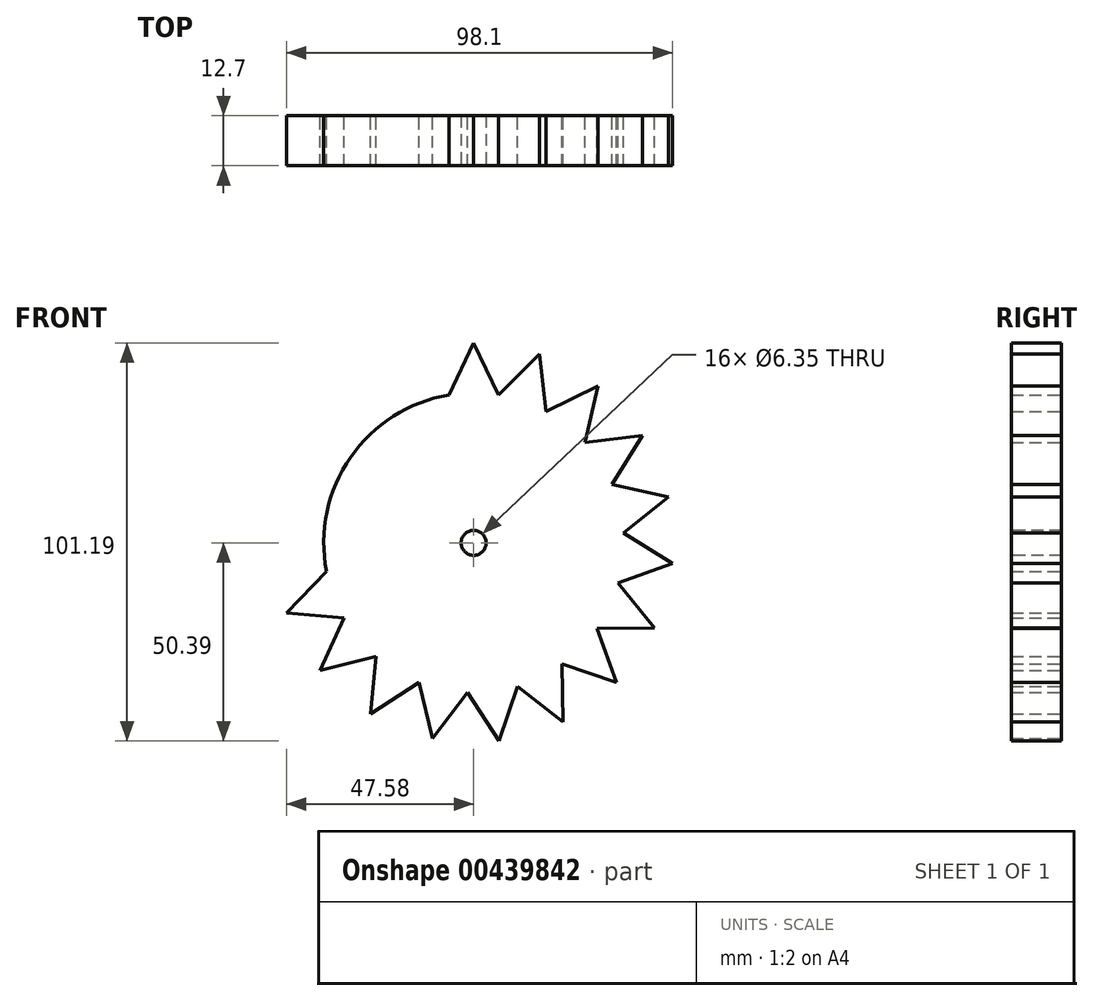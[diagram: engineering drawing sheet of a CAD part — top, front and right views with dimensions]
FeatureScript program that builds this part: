
annotation { "Feature Type Name" : "Feature", "Feature Type Description" : "" }
export const myFeature = defineFeature(function(context is Context, id is Id, definition is map)
    precondition{}
    {
        {
            var Q0;
            Q0=qCreatedBy(makeId("Front.planeOp"),FACE);
            var sketch = newSketch(context, id + "F0", { "sketchPlane" : qUnion([Q0])});
            skCircle(sketch, "E0", {"center": v(0, 0) * mm, "radius": 38.1 * mm});
            skPoint(sketch, "E1", {"position": v(0, 38.1) * mm});
            skPoint(sketch, "E2", {"position": v(12.52, 35.98) * mm});
            skPoint(sketch, "E3", {"position": v(23.65, 29.87) * mm});
            skPoint(sketch, "E4", {"position": v(32.16, 20.43) * mm});
            skPoint(sketch, "E5", {"position": v(37.09, 8.73) * mm});
            skPoint(sketch, "E6", {"position": v(37.9, -3.97) * mm});
            skPoint(sketch, "E7", {"position": v(34.48, -16.2) * mm});
            skPoint(sketch, "E8", {"position": v(27.24, -26.64) * mm});
            skPoint(sketch, "E9", {"position": v(16.97, -34.11) * mm});
            skPoint(sketch, "E10", {"position": v(4.82, -37.8) * mm});
            skPoint(sketch, "E11", {"position": v(-7.87, -37.28) * mm});
            skPoint(sketch, "E12", {"position": v(-19.68, -32.62) * mm});
            skPoint(sketch, "E13", {"position": v(-29.31, -24.34) * mm});
            skPoint(sketch, "E14", {"position": v(-35.68, -13.35) * mm});
            skLineSegment(sketch, "E15", {"start": v(0, 38.1) * mm, "end": v(0, 50.8) * mm});
            skLineSegment(sketch, "E16", {"start": v(0, 0) * mm, "end": v(12.52, 35.98) * mm});
            skLineSegment(sketch, "E17", {"start": v(0, 0) * mm, "end": v(23.65, 29.87) * mm});
            skLineSegment(sketch, "E18", {"start": v(0, 0) * mm, "end": v(32.16, 20.43) * mm});
            skLineSegment(sketch, "E19", {"start": v(0, 0) * mm, "end": v(37.09, 8.73) * mm});
            skLineSegment(sketch, "E20", {"start": v(0, 0) * mm, "end": v(37.9, -3.97) * mm});
            skLineSegment(sketch, "E21", {"start": v(0, 0) * mm, "end": v(34.48, -16.2) * mm});
            skLineSegment(sketch, "E22", {"start": v(0, 0) * mm, "end": v(27.24, -26.64) * mm});
            skLineSegment(sketch, "E23", {"start": v(0, 0) * mm, "end": v(16.97, -34.11) * mm});
            skLineSegment(sketch, "E24", {"start": v(0, 0) * mm, "end": v(4.82, -37.8) * mm});
            skLineSegment(sketch, "E25", {"start": v(0, 0) * mm, "end": v(-7.87, -37.28) * mm});
            skLineSegment(sketch, "E26", {"start": v(0, 0) * mm, "end": v(-19.68, -32.62) * mm});
            skLineSegment(sketch, "E27", {"start": v(0, 0) * mm, "end": v(-29.31, -24.34) * mm});
            skLineSegment(sketch, "E28", {"start": v(0, 0) * mm, "end": v(-35.68, -13.35) * mm});
            skLineSegment(sketch, "E29", {"start": v(12.52, 35.98) * mm, "end": v(16.7, 47.98) * mm});
            skLineSegment(sketch, "E30", {"start": v(23.65, 29.87) * mm, "end": v(31.54, 39.82) * mm});
            skLineSegment(sketch, "E31", {"start": v(32.16, 20.43) * mm, "end": v(42.87, 27.25) * mm});
            skLineSegment(sketch, "E32", {"start": v(37.09, 8.73) * mm, "end": v(49.45, 11.64) * mm});
            skLineSegment(sketch, "E33", {"start": v(34.48, -16.2) * mm, "end": v(45.98, -21.6) * mm});
            skLineSegment(sketch, "E34", {"start": v(27.24, -26.64) * mm, "end": v(36.32, -35.52) * mm});
            skLineSegment(sketch, "E35", {"start": v(16.97, -34.11) * mm, "end": v(22.63, -45.48) * mm});
            skLineSegment(sketch, "E36", {"start": v(4.82, -37.8) * mm, "end": v(6.43, -50.4) * mm});
            skLineSegment(sketch, "E37", {"start": v(-7.87, -37.28) * mm, "end": v(-10.5, -49.7) * mm});
            skLineSegment(sketch, "E38", {"start": v(-19.68, -32.62) * mm, "end": v(-26.25, -43.5) * mm});
            skLineSegment(sketch, "E39", {"start": v(-29.31, -24.34) * mm, "end": v(-39.08, -32.45) * mm});
            skLineSegment(sketch, "E40", {"start": v(-35.68, -13.35) * mm, "end": v(-47.58, -17.8) * mm});
            skLineSegment(sketch, "E41", {"start": v(37.9, -3.97) * mm, "end": v(50.52, -5.3) * mm});
            skPoint(sketch, "E42", {"position": v(-6.33, 37.57) * mm});
            skPoint(sketch, "E43", {"position": v(6.33, 37.57) * mm});
            skPoint(sketch, "E44", {"position": v(18.32, 33.4) * mm});
            skPoint(sketch, "E45", {"position": v(28.29, 25.53) * mm});
            skPoint(sketch, "E46", {"position": v(35.1, 14.81) * mm});
            skPoint(sketch, "E47", {"position": v(36.7, -10.2) * mm});
            skPoint(sketch, "E48", {"position": v(31.31, -21.7) * mm});
            skPoint(sketch, "E49", {"position": v(22.44, -30.8) * mm});
            skPoint(sketch, "E50", {"position": v(-1.52, -38.07) * mm});
            skPoint(sketch, "E51", {"position": v(-13.95, -35.45) * mm});
            skPoint(sketch, "E52", {"position": v(-24.83, -28.9) * mm});
            skPoint(sketch, "E53", {"position": v(-32.95, -19.13) * mm});
            skPoint(sketch, "E54", {"position": v(-37.4, -7.24) * mm});
            skPoint(sketch, "E55", {"position": v(38.02, 2.45) * mm});
            skPoint(sketch, "E56", {"position": v(11.07, -36.46) * mm});
            skLineSegment(sketch, "E57", {"start": v(-6.33, 37.57) * mm, "end": v(0, 50.8) * mm});
            skLineSegment(sketch, "E58", {"start": v(0, 50.8) * mm, "end": v(6.33, 37.57) * mm});
            skLineSegment(sketch, "E59", {"start": v(6.33, 37.57) * mm, "end": v(16.7, 47.98) * mm});
            skLineSegment(sketch, "E60", {"start": v(16.7, 47.98) * mm, "end": v(18.32, 33.4) * mm});
            skLineSegment(sketch, "E61", {"start": v(18.32, 33.4) * mm, "end": v(31.54, 39.82) * mm});
            skLineSegment(sketch, "E62", {"start": v(31.54, 39.82) * mm, "end": v(28.29, 25.53) * mm});
            skLineSegment(sketch, "E63", {"start": v(28.29, 25.53) * mm, "end": v(42.87, 27.25) * mm});
            skLineSegment(sketch, "E64", {"start": v(42.87, 27.25) * mm, "end": v(35.1, 14.81) * mm});
            skLineSegment(sketch, "E65", {"start": v(35.1, 14.81) * mm, "end": v(49.45, 11.64) * mm});
            skLineSegment(sketch, "E66", {"start": v(49.45, 11.64) * mm, "end": v(38.02, 2.45) * mm});
            skLineSegment(sketch, "E67", {"start": v(38.02, 2.45) * mm, "end": v(50.52, -5.3) * mm});
            skLineSegment(sketch, "E68", {"start": v(50.52, -5.3) * mm, "end": v(36.7, -10.2) * mm});
            skLineSegment(sketch, "E69", {"start": v(36.7, -10.2) * mm, "end": v(45.98, -21.6) * mm});
            skLineSegment(sketch, "E70", {"start": v(45.98, -21.6) * mm, "end": v(31.31, -21.7) * mm});
            skLineSegment(sketch, "E71", {"start": v(31.31, -21.7) * mm, "end": v(36.32, -35.52) * mm});
            skLineSegment(sketch, "E72", {"start": v(36.32, -35.52) * mm, "end": v(22.44, -30.8) * mm});
            skLineSegment(sketch, "E73", {"start": v(22.44, -30.8) * mm, "end": v(22.63, -45.48) * mm});
            skLineSegment(sketch, "E74", {"start": v(22.63, -45.48) * mm, "end": v(11.07, -36.46) * mm});
            skLineSegment(sketch, "E75", {"start": v(11.07, -36.46) * mm, "end": v(6.43, -50.4) * mm});
            skLineSegment(sketch, "E76", {"start": v(6.43, -50.4) * mm, "end": v(-1.52, -38.07) * mm});
            skLineSegment(sketch, "E77", {"start": v(-1.52, -38.07) * mm, "end": v(-10.5, -49.7) * mm});
            skLineSegment(sketch, "E78", {"start": v(-10.5, -49.7) * mm, "end": v(-13.95, -35.45) * mm});
            skLineSegment(sketch, "E79", {"start": v(-13.95, -35.45) * mm, "end": v(-26.25, -43.5) * mm});
            skLineSegment(sketch, "E80", {"start": v(-26.25, -43.5) * mm, "end": v(-24.83, -28.9) * mm});
            skLineSegment(sketch, "E81", {"start": v(-24.83, -28.9) * mm, "end": v(-39.08, -32.45) * mm});
            skLineSegment(sketch, "E82", {"start": v(-39.08, -32.45) * mm, "end": v(-32.95, -19.13) * mm});
            skLineSegment(sketch, "E83", {"start": v(-32.95, -19.13) * mm, "end": v(-47.58, -17.8) * mm});
            skLineSegment(sketch, "E84", {"start": v(-47.58, -17.8) * mm, "end": v(-37.4, -7.24) * mm});
            skSolve(sketch);
        }
        {
            var Q0;
            Q0=qSketchRegion(id+"F0",true);
            extrude(context, id + "F1", {"entities" : qUnion([Q0]), "depth" : 12.7 * mm});
        }
        {
            var Q0;
            Q0=makeQuery(id+"F1.opExtrude","CAP_FACE",FACE,{"disambiguationData":[OSD([sQuery(id+"F0.wireOp",EDGE,"E0"),sQuery(id+"F0.wireOp",EDGE,"E57"),sQuery(id+"F0.wireOp",EDGE,"E58"),sQuery(id+"F0.wireOp",EDGE,"E59"),sQuery(id+"F0.wireOp",EDGE,"E60"),sQuery(id+"F0.wireOp",EDGE,"E61"),sQuery(id+"F0.wireOp",EDGE,"E62"),sQuery(id+"F0.wireOp",EDGE,"E63"),sQuery(id+"F0.wireOp",EDGE,"E64"),sQuery(id+"F0.wireOp",EDGE,"E65"),sQuery(id+"F0.wireOp",EDGE,"E66"),sQuery(id+"F0.wireOp",EDGE,"E67"),sQuery(id+"F0.wireOp",EDGE,"E68"),sQuery(id+"F0.wireOp",EDGE,"E69"),sQuery(id+"F0.wireOp",EDGE,"E70"),sQuery(id+"F0.wireOp",EDGE,"E71"),sQuery(id+"F0.wireOp",EDGE,"E72"),sQuery(id+"F0.wireOp",EDGE,"E73"),sQuery(id+"F0.wireOp",EDGE,"E74"),sQuery(id+"F0.wireOp",EDGE,"E75"),sQuery(id+"F0.wireOp",EDGE,"E76"),sQuery(id+"F0.wireOp",EDGE,"E77"),sQuery(id+"F0.wireOp",EDGE,"E78"),sQuery(id+"F0.wireOp",EDGE,"E79"),sQuery(id+"F0.wireOp",EDGE,"E80"),sQuery(id+"F0.wireOp",EDGE,"E81"),sQuery(id+"F0.wireOp",EDGE,"E82"),sQuery(id+"F0.wireOp",EDGE,"E83"),sQuery(id+"F0.wireOp",EDGE,"E84")])],"isStart":false});
            var sketch = newSketch(context, id + "F2", { "sketchPlane" : qUnion([Q0])});
            skCircle(sketch, "E85", {"center": v(0, 0) * mm, "radius": 3.18 * mm});
            skSolve(sketch);
        }
        {
            var Q0;
            Q0=makeQuery(id+"F2.imprint","IMPRINT",FACE,{"disambiguationData":[TD([[makeQuery(id+"F2.imprint","IMPRINT",EDGE,{"derivedFrom":sQuery(id+"F2.wireOp",EDGE,"E85")}),1.0]])]});
            extrude(context, id + "F3", {"entities" : qUnion([Q0]), "operationType" : NewBodyOperationType.REMOVE, "oppositeDirection" : true, "depth" : 25.4 * mm});
        }
    });
